# Revit family: equip-sink-elkay-surg-wall-eslvafc
name_source: partatom
category: Plumbing Fixtures
units: mm (PartAtom-declared; Revit-internal decimal feet)

## family parameters
Cut with Voids When Loaded = No
Host = Face
Part Type = Normal
Room Calculation Point = No
Round Connector Dimension = Use Radius
Shared = No

## types (1)
- ESLV2820FC
    AC Power = No
    Assembly Code = D2010410
    Back of Side Bowls to Back of Sink = 0' - 3"
    Backsplash Height = 1' - 0"
    Bowl Depth = 0' - 7 1/2"
    Bowl Drain Location FB = 0' - 6"
    Bowl Length = 1' - 2"
    Bowl Width = 1' - 0"
    Bubbler CW Flow Rate = 2 GPM
    Bubbler Material = Metal - Steel - Stainless - Chrome
    Bubbler Nominal Dia = 0' - 0 1/2"
    Bubbler Nominal Radius = 0' - 0 1/4"
    CW Flow Rate = 2 GPM
    CWFU = 0
    Cost = 1 $
    Default Elevation = 3' - 0"
    Description = Wash-Up Lavatory Sinks
    Drain CL LR to Left Bowl Edge = 0' - 7"
    Drain Material = Metal - Steel - Stainless - Chrome
    Faucet CL to Back of Sink = 0' - 3 3/16"
    Faucet Hole Dia = 0' - 1 1/4"
    Faucet Hole One = No
    Faucet Hole One Top = 0' - 0 1/8"
    Faucet Hole One to CL = 0' - 4"
    Faucet Hole Three = No
    Faucet Hole Three Top = 0' - 0 1/8"
    Faucet Hole Two = Yes
    Faucet Hole Two Top = 0' - 0 1/4"
    Faucet Material = Metal - Steel - Stainless - Chrome
    Faucet Part = LK396A
    Faucet Water Supply Radius = 0' - 0 3/16"
    HW Flow Rate = 2 GPM
    HWFU = 0
    Hole One to Three = 0' - 8"
    Hole One to Two = 0' - 4"
    Hole Radius = 0' - 0 5/8"
    Keynote = D2010410
    Left Bowl Dist to Left Sink Edge = 0' - 2"
    Left Partition Width = 0' - 1 1/4"
    Manufacturer = Elkay Manufacturing
    MasterFormat Number = 22.42.16.16
    MasterFormat Title = Commercial Sinks
    Mechanical Mix Valve = No
    Mix Valve Part = LK398C
    Model = ESLV2820FC
    No Mix Valve = No
    Nominal Dia = 0' - 0 1/2"
    Nominal Radius = 0' - 0 1/4"
    OmniClass Code = 23.45.05.14.14.27
    OmniClass Title = Service Sinks
    Overflow Void = 0' - 0 1/16"
    Reference Level to Back Plane = 0' - 1 1/2"
    Right Bowl Dist to Right Sink Edge = 0' - 2"
    Right Partition Width = 0' - 1 1/4"
    Rough-In Sanitary Installation Height = 1' - 9"
    Rough-In Sanitary Left From CL Sink = 0' - 2"
    Rough-In Water Supply Distance Right from CL Sink = 0' - 4"
    Rough-In Water Supply Installation Height = 0' - 11 7/8"
    Sanitary Flow Rate = 10 GPM
    Sanitary Nominal Dia = 0' - 1 1/2"
    Sanitary Nominal Radius = 0' - 0 3/4"
    Sink Deck to Faucet Water Inlet = 1' - 4 5/8"
    Sink Ledge Back Width = 0' - 5"
    Sink Ledge Back Width Hidden = 0' - 5"
    Sink Ledge Front Width = 0' - 3"
    Sink Ledge Front Width Hidden = 0' - 3"
    Sink Ledge Left Width = 0' - 7"
    Sink Ledge Left Width Hidden = 0' - 7"
    Sink Ledge Right Width = 0' - 7"
    Sink Ledge Right Width Hidden = 0' - 7"
    Sink Length = 2' - 4"
    Sink Material = Metal - Steel - Stainless - Chrome
    Sink Part = ESLV28201
    Sink San Conn Extr Visibility = No
    Sink Width = 1' - 8"
    Special Mix Valve = Yes
    Specification Sheet URL = http://www.elkayusa.com
    Stem Material = Metal - Steel
    Supply Line Mix Length = 0' - 0 1/2"
    Thermostatic Mix Valve = No
    URL = www.elkayusa.com
    Valve Material = Metal - Steel - Stainless - Chrome
    Vent Connection = Yes
    WFU = 0

## geometry (parser evidence)
native form markers: Sweep x18
no freeform markers — native parametric forms only
